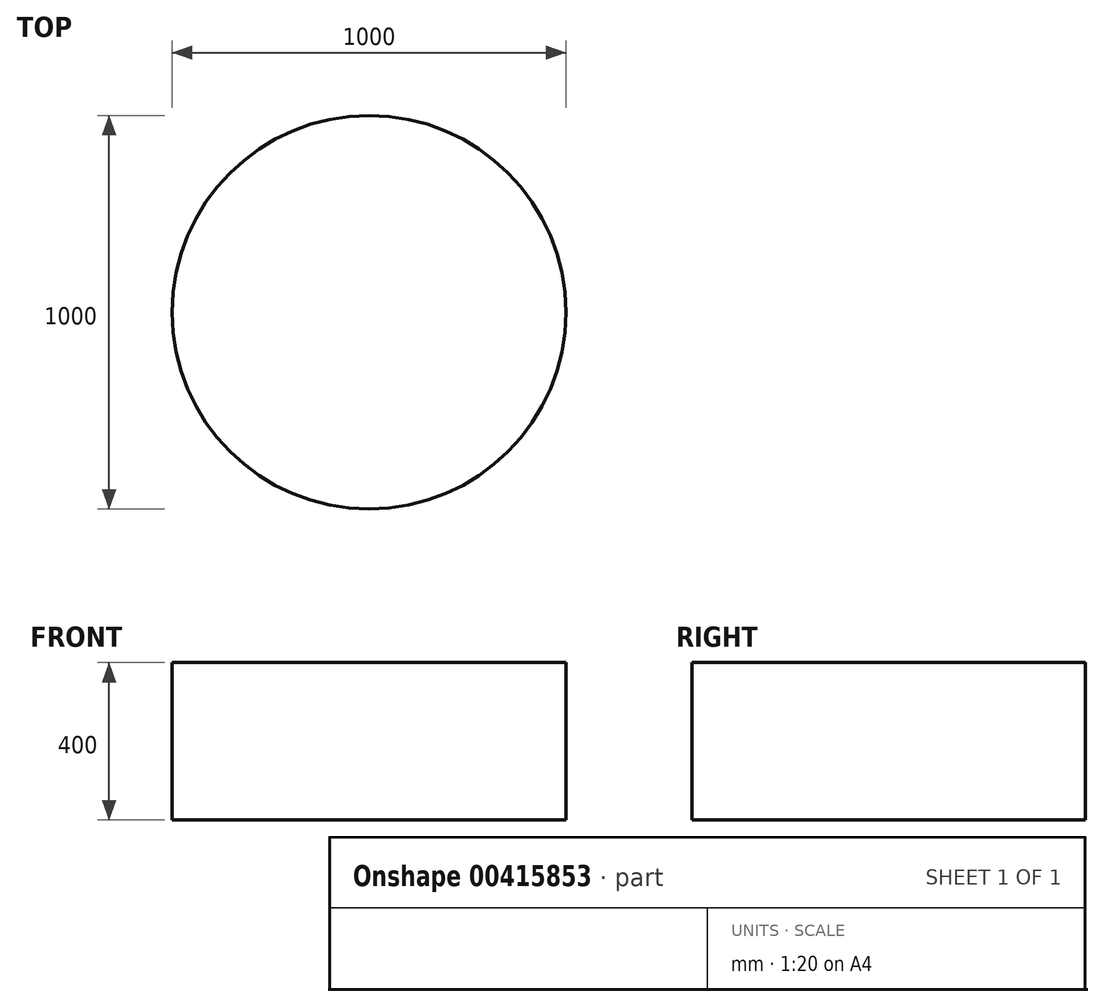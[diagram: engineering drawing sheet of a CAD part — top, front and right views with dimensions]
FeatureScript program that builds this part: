
annotation { "Feature Type Name" : "Feature", "Feature Type Description" : "" }
export const myFeature = defineFeature(function(context is Context, id is Id, definition is map)
    precondition{}
    {
        {
            var Q0;
            Q0=qCreatedBy(makeId("Top.planeOp"),FACE);
            var sketch = newSketch(context, id + "F0", { "sketchPlane" : qUnion([Q0])});
            skCircle(sketch, "E0", {"center": v(0, 0) * mm, "radius": 500 * mm});
            skSolve(sketch);
        }
        {
            var Q0;
            Q0=makeQuery(id+"F0.imprint","IMPRINT",FACE,{"disambiguationData":[TD([[makeQuery(id+"F0.imprint","IMPRINT",EDGE,{"derivedFrom":sQuery(id+"F0.wireOp",EDGE,"E0")}),1.0]])]});
            extrude(context, id + "F1", {"entities" : qUnion([Q0]), "depth" : 400 * mm});
        }
    });
